# Revit family: 0053415
name_source: partatom
category: Lighting Fixtures
revit_build: Autodesk Revit 2017 (Build: 20160225_1515(x64)
units: mm (PartAtom-declared; Revit-internal decimal feet)

## family parameters
Cut with Voids When Loaded = No
Host = Face
Light Source = Yes
OmniClass Number = 23.80.70.00
OmniClass Title = Lighting
Part Type = Normal
Room Calculation Point = No
Round Connector Dimension = Use Diameter
Shared = No

## types (3) — shared parameters
Apparent Load = 18 VA
Assembly Code = D5020200
AssetType = Fixed
ClassificationName = Uniclass2015
ClassificationValue = EF_70_80
Color Filter = 16777215
Default Elevation = 1219 mm
Dimming Lamp Color Temperature Shift = <None>
DocumentationLiterature = http://www.sylvania-lighting.com
ElectricShockClassification = Class II
Emit Shape Visible in Rendering = No
Emit from Circle Diameter = 249 mm
IfcExportAs = IfcLightFixtureType
IfcExportType = IfcLightFixtureType
ImpactProtectionIndex = IK03
IngressProtection = IP20
InputNominalFrequency = 50/60 Hz
InputVoltage = 220-240 V AC
Keynote = 16500
Lamp = LED
LampColourRenderingIndex = 80
LampNominalLuminous = 1900 lm
LampsType = LED
LuminousAreaRad_SYL = 124 mm
LuminousEfficacy = 106 lm/W
M_SYL = No
Manufacturer = Feilo Sylvania
ManufacturerName = Feilo Sylvania
Material = pc polycarbonate housing
Material_1_SYL = PC/ABS Plastic
Material_2_SYL = LED
Material_3_SYL = Chrome - Polished
Material_4_SYL = Plastic, Opaque Black
ModelNumber = 0053415
NominalDepth = 290 mm  [stored 0.951444 ft]
NominalHeight = 35 mm  [stored 0.114829 ft]
NominalLength = 290 mm  [stored 0.951444 ft]
PowerConsumption = 18 W
RadiusRingIn_SYL = 123 mm
RadiusRing_SYL = 147 mm
Radius_SYL = 146 mm
S_SYL = No
Tilt Angle = -90.00°
Type Image = <None>
URL = http://www.sylvania-lighting.com
Voltage = 230 V
Weight = 5.76 kg
zero-valued in all types: Cost, PowerFactor

## per-type parameters (varying)
| type | LampColourTemperature | Model | ModelReference | Name | Photometric Web File | TypeName |
| 0053415 SYLFLAT 5IN1 55-250 1900LM CCT LILO - 6500K | 6500 K | SYLFLAT 5IN1 55-250 1900LM CCT LILO - 6500K | SYLFLAT 5IN1 55-250 1900LM CCT LILO - 6500K | SYLFLAT 5IN1 55-250 1900LM CCT LILO - 6500K | 0053415-WW.ies | SYLFLAT 5IN1 55-250 1900LM CCT LILO - 6500K |
| 0053415 SYLFLAT 5IN1 55-250 1900LM CCT LILO - 4000K | 4000 K | SYLFLAT 5IN1 55-250 1900LM CCT LILO - 4000K | SYLFLAT 5IN1 55-250 1900LM CCT LILO - 4000K | SYLFLAT 5IN1 55-250 1900LM CCT LILO - 4000K | 0053415-NW.ies | SYLFLAT 5IN1 55-250 1900LM CCT LILO - 4000K |
| 0053415 SYLFLAT 5IN1 55-250 1900LM CCT LILO - 3000K | 3000 K | SYLFLAT 5IN1 55-250 1900LM CCT LILO - 3000K | SYLFLAT 5IN1 55-250 1900LM CCT LILO - 3000K | SYLFLAT 5IN1 55-250 1900LM CCT LILO - 3000K | 0053415-CW.ies | SYLFLAT 5IN1 55-250 1900LM CCT LILO - 3000K |

note: [stored X ft] marks values corroborated as IEEE doubles in the binary element streams (Revit-internal decimal feet)

## geometry (parser evidence)
native form markers: Sweep x3
no freeform markers — native parametric forms only
